# Revit family: Drain_Floor_13.5_ Inch_Square_Extra-Heavy-Duty-Zurn-Z676
name_source: partatom
category: Plumbing Fixtures
units: mm (PartAtom-declared; Revit-internal decimal feet)

## family parameters
Always vertical = Yes
Cut with Voids When Loaded = No
Maintain Annotation Orientation = No
OmniClass Number = 23.70.50.21.24
OmniClass Title = Waste Water Drains
Part Type = Normal
Room Calculation Point = No
Round Connector Dimension = Use Radius
Shared = No
Work Plane-Based = No

## types (18) — shared parameters
Approx. Weight (Lbs) = 95
Assembly Code = D2030300
CW Connection = No
Default Elevation = 0' - 0"
Description = 13-1/2 Square Extra Heavy-Duty Drain
Frame = 0' - 6"
HW Connection = No
Main Material = Iron - Zurn - Cast - Painted - Blue
Manufacturer = Zurn Water, LLC
Manufacurer Brand = Zurn
Model = Z676
Product Documentation Link = https://files.zurn.com
Product Page URL = https://www.zurn.com
Product data url = https://www.bimobject.com
URL = www.zurn.com
Vent Connection = No

## per-type parameters (varying)
| type | Body Height | Frame Height | Frame Width | Outlet Outer Radius | Outlet Radius | Top | Type Comments |
| Z676-4IC Outlet | 0' - 9 1/8" | 0' - 1" | 1' - 1 1/2" | 0' - 2 27/32" | 0' - 2" | Iron - Zurn - Cast - Painted - Blue | Z676-4IC (Inside Caulk Outlet) |
| Z676-4IP Outlet | 0' - 9 1/8" | 0' - 1" | 1' - 1 1/2" | 0' - 2 27/32" | 0' - 2" | Iron - Zurn - Cast - Painted - Blue | Z676-4IP (Threaded Outlet) |
| Z676-3IP Outlet | 0' - 9 1/8" | 0' - 1" | 1' - 1 1/2" | 0' - 2 11/32" | 0' - 1 1/2" | Iron - Zurn - Cast - Painted - Blue | Z676-3IP (Threaded Outlet) |
| Z676-6IP Outlet | 0' - 9 1/8" | 0' - 1" | 1' - 1 1/2" | 0' - 3 27/32" | 0' - 3" | Iron - Zurn - Cast - Painted - Blue | Z676-6IP (Threaded Outlet) |
| Z676-4NH Outlet | 0' - 9 3/8" | 0' - 1" | 1' - 1 1/2" | 0' - 2 5/32" | 0' - 2" | Iron - Zurn - Cast - Painted - Blue | Z676-4NH (No Hub Outlet) IP w/Z1040 |
| Z676-3NH Outlet | 0' - 9 1/2" | 0' - 1" | 1' - 1 1/2" | 0' - 1 21/32" | 0' - 1 1/2" | Iron - Zurn - Cast - Painted - Blue | Z676-3NH (No Hub Outlet) IP w/Z1040 |
| Z676-3NL Outlet | 0' - 8 1/2" | 0' - 1" | 1' - 1 1/2" | 0' - 1 21/32" | 0' - 1 1/2" | Iron - Zurn - Cast - Painted - Blue | Z676-3NL (Neo-Loc Outlet) |
| Z676-4NL Outlet | 0' - 8 1/2" | 0' - 1" | 1' - 1 1/2" | 0' - 2 25/32" | 0' - 2" | Iron - Zurn - Cast - Painted - Blue | Z676-4NL (Neo-Loc Outlet) |
| ZN676-4IC Outlet | 0' - 9 5/8" | 0' - 1 3/16" | 1' - 2 3/16" | 0' - 2 27/32" | 0' - 2" | Bronze - Polished Nickel | ZN676-4IC (Inside Caulk Outlet) |
| ZN676-3IP Outlet | 0' - 9 5/8" | 0' - 1 3/16" | 1' - 2 3/16" | 0' - 2 11/32" | 0' - 1 1/2" | Bronze - Polished Nickel | ZN676-3IP (Threaded Outlet) |
| ZN676-4IP Outlet | 0' - 9 5/8" | 0' - 1 3/16" | 1' - 2 3/16" | 0' - 2 27/32" | 0' - 2" | Bronze - Polished Nickel | ZN676-4IP (Threaded Outlet) |
| ZN676-3NH Outlet | 0' - 9 1/2" | 0' - 1 3/16" | 1' - 2 3/16" | 0' - 1 21/32" | 0' - 1 1/2" | Bronze - Polished Nickel | ZN676-3NH (No Hub Outlet) IP w/Z1040 |
| ZN676-3NL Outlet | 0' - 8 1/2" | 0' - 1 3/16" | 1' - 2 3/16" | 0' - 1 21/32" | 0' - 1 1/2" | Bronze - Polished Nickel | ZN676-3NL (No Hub Outlet) |
| ZN676-6IP Outlet | 0' - 9 5/8" | 0' - 1 3/16" | 1' - 2 3/16" | 0' - 3 27/32" | 0' - 3" | Bronze - Polished Nickel | ZN676-6IP (Threaded Outlet) |
| ZN676-4NH Outlet | 0' - 9 3/8" | 0' - 1 3/16" | 1' - 2 3/16" | 0' - 3 27/32" | 0' - 3" | Bronze - Polished Nickel | ZN676-4NH (No Hub Outlet) IP w/Z1040 |
| ZN676-4NL Outlet | 0' - 8 1/2" | 0' - 1 3/16" | 1' - 2 3/16" | 0' - 2 25/32" | 0' - 2" | Bronze - Polished Nickel | ZN676-4NL (Neo-Loc Outlet) |
| ZN676-6NH Outlet | 0' - 9 1/4" | 0' - 1 3/16" | 1' - 2 3/16" | 0' - 3 1/8" | 0' - 3" | Bronze - Polished Nickel | ZN676-6NH (No Hub Outlet) IP w/Z1040 |
| Z676-6NH Outlet | 0' - 9 1/4" | 0' - 1" | 1' - 1 1/2" | 0' - 3 1/8" | 0' - 3" | Iron - Zurn - Cast - Painted - Blue | Z676-6NH (No Hub Outlet) IP w/Z1040 |

## geometry (parser evidence)
native form markers: Sweep x4
no freeform markers — native parametric forms only
